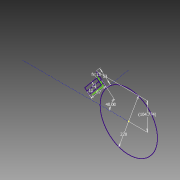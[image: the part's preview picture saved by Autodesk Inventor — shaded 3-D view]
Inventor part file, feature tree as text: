
AUTODESK INVENTOR PART (.ipt)
format: ipt  version: 2015 (Build 190159000, 159)  size: 73,216 bytes
history: native  units: mm
features: sketch x1
ambient origin geometry x8: Origin, YZ Plane, XZ Plane, XY Plane, X Axis, Y Axis, Z Axis, Center Point
feature tree (1):
  sketch  "Sketch1"  dims[d0=220.0mm d1=53.0mm d2=87.0mm d3=6.981317mm d4=104.77438mm d5=11.0mm d6=22.0mm d8=15.0mm]
